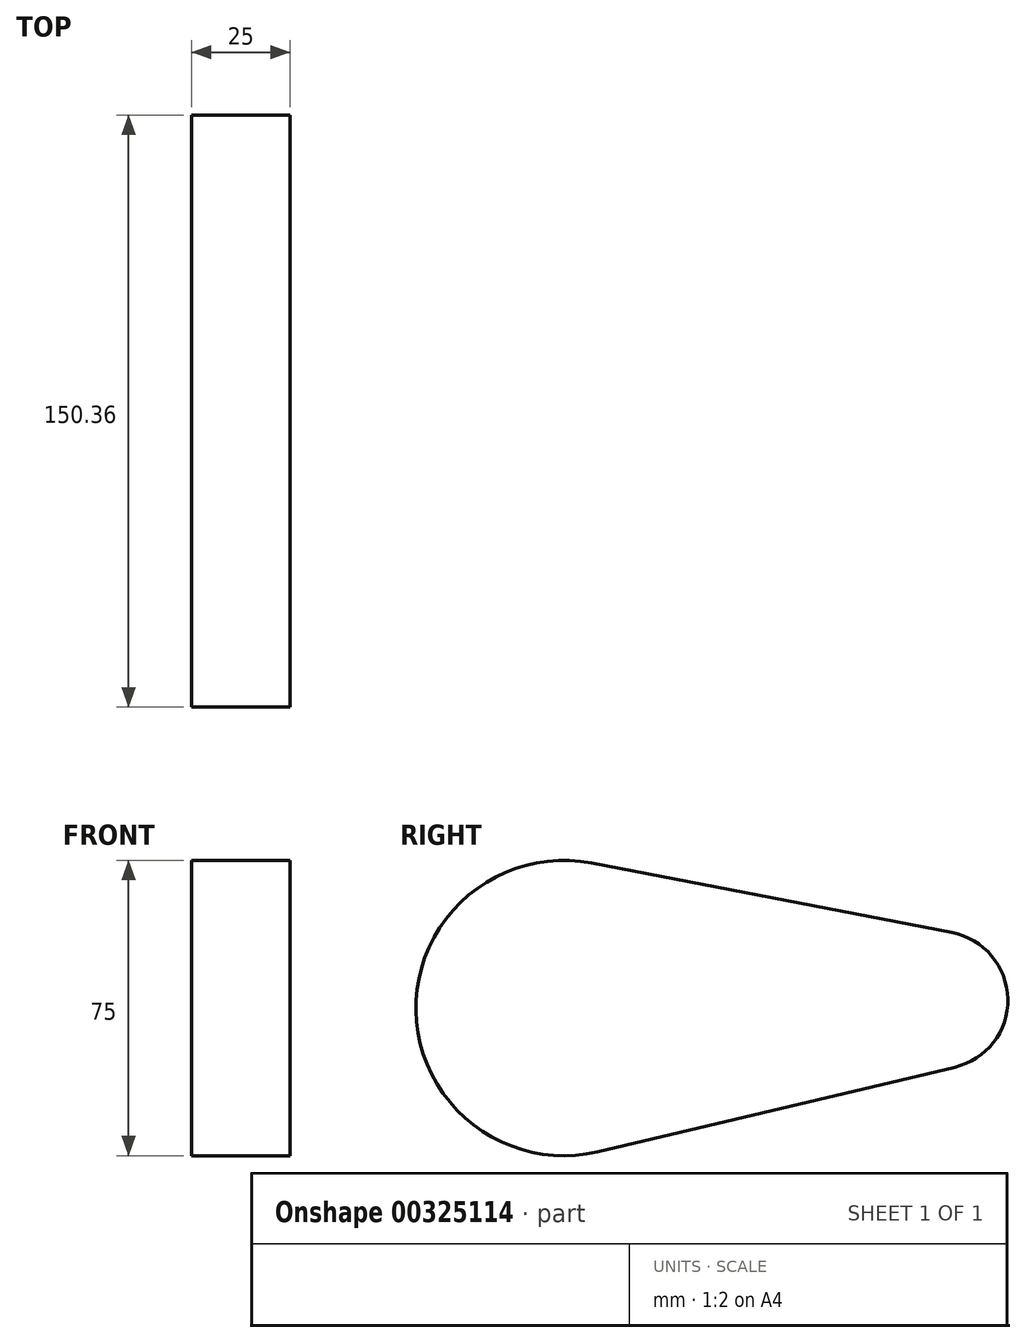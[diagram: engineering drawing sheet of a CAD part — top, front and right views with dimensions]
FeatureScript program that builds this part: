
annotation { "Feature Type Name" : "Feature", "Feature Type Description" : "" }
export const myFeature = defineFeature(function(context is Context, id is Id, definition is map)
    precondition{}
    {
        {
            var Q0;
            Q0=qCreatedBy(makeId("Right.planeOp"),FACE);
            var sketch = newSketch(context, id + "F0", { "sketchPlane" : qUnion([Q0])});
            skArc(sketch, "E0", {"start": v(18.06, 36.82) * mm, "mid": v(-26.54, -0.78) * mm, "end": v(19.58, -36.5) * mm});
            skArc(sketch, "E1", {"start": v(110.34, -15.05) * mm, "mid": v(123.82, 2.35) * mm, "end": v(109.63, 19.17) * mm});
            skLineSegment(sketch, "E2", {"start": v(109.63, 19.17) * mm, "end": v(18.06, 36.82) * mm});
            skLineSegment(sketch, "E3", {"start": v(19.58, -36.5) * mm, "end": v(110.34, -15.05) * mm});
            skSolve(sketch);
        }
        {
            var Q0;
            Q0 = qSketchRegion(id + "F0", true);
            extrude(context, id + "F1", {"entities" : qUnion([Q0]), "depth" : 25 * mm});
        }
    });
